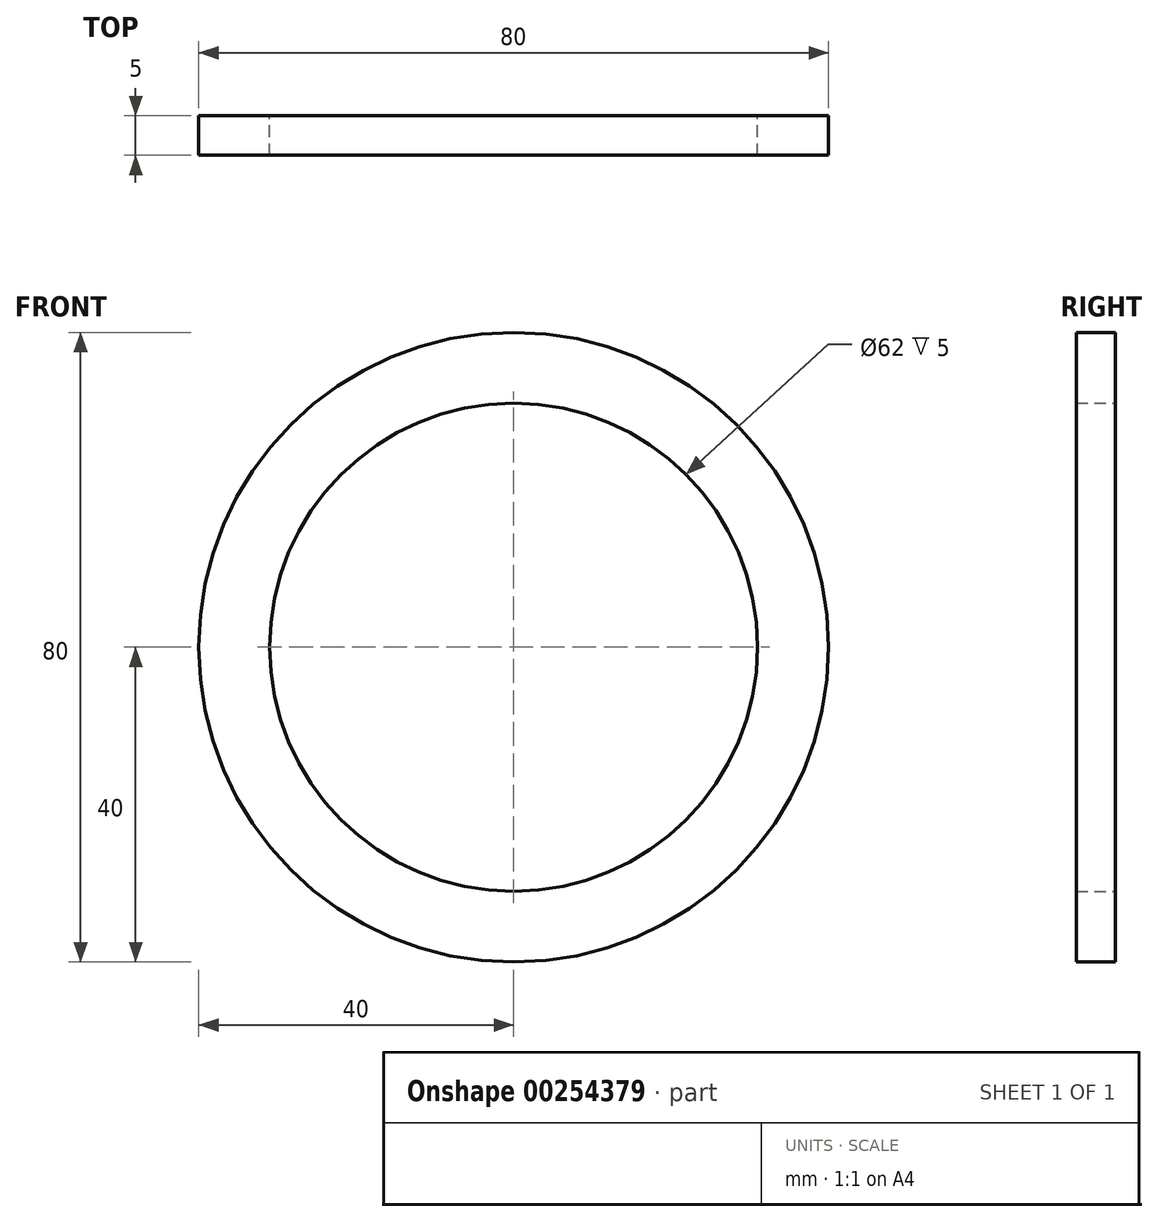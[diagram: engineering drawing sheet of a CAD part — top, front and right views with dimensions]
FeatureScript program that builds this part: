
annotation { "Feature Type Name" : "Feature", "Feature Type Description" : "" }
export const myFeature = defineFeature(function(context is Context, id is Id, definition is map)
    precondition{}
    {
        {
            var Q0;
            Q0=qCreatedBy(makeId("Front.planeOp"),FACE);
            var sketch = newSketch(context, id + "F0", { "sketchPlane" : qUnion([Q0])});
            skCircle(sketch, "E0", {"center": v(0, 0) * mm, "radius": 40 * mm});
            skCircle(sketch, "E1", {"center": v(0, 0) * mm, "radius": 31 * mm});
            skCircle(sketch, "E2", {"center": v(0, 0) * mm, "radius": 7.5 * mm});
            skCircle(sketch, "E3", {"center": v(0, 0) * mm, "radius": 2.5 * mm});
            skLineSegment(sketch, "E4", {"start": v(0, 0) * mm, "end": v(0, 40) * mm});
            skLineSegment(sketch, "E5", {"start": v(0, 0) * mm, "end": v(0, -40) * mm});
            skLineSegment(sketch, "E6", {"start": v(0, 0) * mm, "end": v(40, 0) * mm});
            skLineSegment(sketch, "E7", {"start": v(0, 0) * mm, "end": v(-40, 0) * mm});
            skLineSegment(sketch, "E8.0", {"start": v(-5, 0) * mm, "end": v(-5, 40) * mm});
            skLineSegment(sketch, "E9.0", {"start": v(5, 0) * mm, "end": v(5, 40) * mm});
            skLineSegment(sketch, "E10.0", {"start": v(0, -5) * mm, "end": v(40, -5) * mm});
            skLineSegment(sketch, "E11.0", {"start": v(0, 5) * mm, "end": v(40, 5) * mm});
            skLineSegment(sketch, "E12.0", {"start": v(-5, 0) * mm, "end": v(-5, -40) * mm});
            skLineSegment(sketch, "E13.0", {"start": v(5, 0) * mm, "end": v(5, -40) * mm});
            skLineSegment(sketch, "E14.0", {"start": v(0, 5) * mm, "end": v(-40, 5) * mm});
            skLineSegment(sketch, "E15.0", {"start": v(0, -5) * mm, "end": v(-40, -5) * mm});
            skSolve(sketch);
        }
        {
            var Q0;
            Q0 = qSketchRegion(id + "F0", true);
            extrude(context, id + "F1", {"entities" : qUnion([Q0]), "depth" : 5 * mm, "offsetDistance" : 25 * mm});
        }
    });
